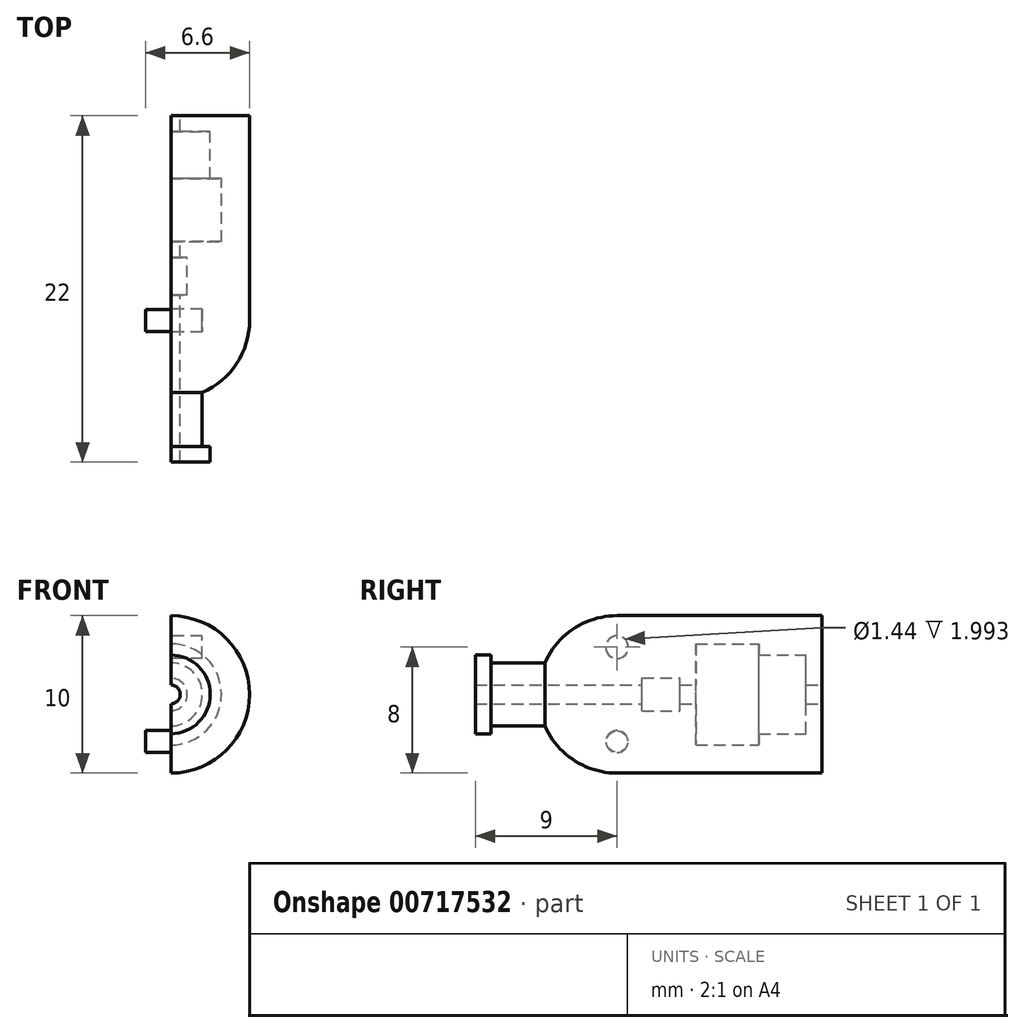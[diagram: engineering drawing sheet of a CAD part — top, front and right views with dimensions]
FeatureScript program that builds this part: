
annotation { "Feature Type Name" : "Feature", "Feature Type Description" : "" }
export const myFeature = defineFeature(function(context is Context, id is Id, definition is map)
    precondition{}
    {
        {
            var Q0;
            Q0=qCreatedBy(makeId("Front.planeOp"),FACE);
            var sketch = newSketch(context, id + "F0", { "sketchPlane" : qUnion([Q0])});
            skLineSegment(sketch, "E0", {"start": v(0, 5) * mm, "end": v(0, 5) * mm});
            skArc(sketch, "E1", {"start": v(0.01, -5) * mm, "mid": v(5, 0) * mm, "end": v(0, 5) * mm});
            skArc(sketch, "E2", {"start": v(0, 5) * mm, "mid": v(-5, 0) * mm, "end": v(0.01, -5) * mm});
            skLineSegment(sketch, "E3", {"start": v(0.01, -5) * mm, "end": v(0.01, -5) * mm});
            skLineSegment(sketch, "E4", {"start": v(0, 5) * mm, "end": v(0.01, -5) * mm});
            skSolve(sketch);
        }
        {
            var Q0;
            Q0=qCreatedBy(makeId("Front.planeOp"),FACE);
            var sketch = newSketch(context, id + "F1", { "sketchPlane" : qUnion([Q0])});
            skCircle(sketch, "E5", {"center": v(0, 0) * mm, "radius": 2 * mm});
            skSolve(sketch);
        }
        {
            var Q0;
            Q0=qCreatedBy(makeId("Front.planeOp"),FACE);
            var sketch = newSketch(context, id + "F2", { "sketchPlane" : qUnion([Q0])});
            skCircle(sketch, "E6", {"center": v(0, 0) * mm, "radius": 2.5 * mm});
            skSolve(sketch);
        }
        {
            var Q0;
            Q0 = qSketchRegion(id + "F0", true);
            var Q1;
            Q1 = qSketchRegion(id + "F10", true);
            extrude(context, id + "F3", {"entities" : qUnion([Q0, Q1]), "depth" : 18 * mm, "offsetDistance" : 25 * mm});
        }
        {
            var Q0;
            Q0=makeQuery(id+"F3.opExtrude","CAP_FACE",FACE,{"disambiguationData":[OSD([sQuery(id+"F0.wireOp",EDGE,"hpv3EBvw-azX5-sWzc-IP0I-4SNIJudsjbpc")])],"isStart":true});
            var Q1;
            Q1=makeQuery(id+"F3.opExtrude","CAP_FACE",FACE,{"disambiguationData":[OSD([sQuery(id+"F0.wireOp",EDGE,"E1"),sQuery(id+"F0.wireOp",EDGE,"E2")])],"isStart":false});
            fillet(context, id + "F4", {"entities" : qUnion([Q0, Q1]), "radius" : 5 * mm, "tangentPropagation" : true, "allowEdgeOverflow" : false});
        }
        {
            var Q0;
            Q0 = qSketchRegion(id + "F1", true);
            extrude(context, id + "F5", {"entities" : qUnion([Q0]), "operationType" : NewBodyOperationType.ADD, "depth" : 21 * mm, "offsetDistance" : 25 * mm, "hasSecondDirection" : true, "secondDirectionOppositeDirection" : false, "secondDirectionDepth" : 16 * mm});
        }
        {
            var Q0;
            Q0=makeQuery(id+"F2.imprint","IMPRINT",FACE,{"disambiguationData":[TD([[makeQuery(id+"F2.imprint","IMPRINT",EDGE,{"derivedFrom":sQuery(id+"F2.wireOp",EDGE,"E6")}),1.0]])]});
            extrude(context, id + "F6", {"entities" : qUnion([Q0]), "operationType" : NewBodyOperationType.ADD, "depth" : 22 * mm, "offsetDistance" : 25 * mm, "hasSecondDirection" : true, "secondDirectionOppositeDirection" : false, "secondDirectionDepth" : 21 * mm});
        }
        {
            var Q0;
            Q0=makeQuery(id+"F0.imprint","IMPRINT",FACE,{"disambiguationData":[TD([[makeQuery(id+"F0.imprint","IMPRINT",EDGE,{"derivedFrom":sQuery(id+"F0.wireOp",EDGE,"E2")}),1.0]])]});
            var Q1;
            Q1=sQuery(id+"F0.wireOp",EDGE,"E2");
            extrude(context, id + "F7", {"entities" : qUnion([Q0]), "operationType" : NewBodyOperationType.REMOVE, "surfaceEntities" : qUnion([Q1]), "endBound" : BoundingType.SYMMETRIC, "oppositeDirection" : true, "depth" : 46 * mm, "offsetDistance" : 25 * mm});
        }
        {
            var Q0;
            Q0=makeQuery(id+"F0.imprint","IMPRINT",FACE,{"disambiguationData":[TD([[makeQuery(id+"F0.imprint","IMPRINT",EDGE,{"derivedFrom":sQuery(id+"F0.wireOp",EDGE,"E1")}),1.0]])]});
            var sketch = newSketch(context, id + "F8", { "sketchPlane" : qUnion([Q0])});
            skCircle(sketch, "E7", {"center": v(0, 0) * mm, "radius": 3.22 * mm});
            skSolve(sketch);
        }
        {
            var Q0;
            {var subQ0=sQuery(id+"F8.wireOp",EDGE,"E7");var subQ1=makeQuery(id+"F0.imprint","IMPRINT",EDGE,{"derivedFrom":sQuery(id+"F0.wireOp",EDGE,"E4")});var subQ2=makeQuery(id+"F8.imprint","INTERSECT",VERTEX,{"disambiguationData":[OD(0.0)],"derivedFrom":[subQ1,subQ0]});Q0=makeQuery(id+"F8.imprint","IMPRINT",FACE,{"disambiguationData":[TD([[makeQuery(id+"F8.imprint","IMPRINT",EDGE,{"disambiguationData":[TD([[subQ2,-1.0]])],"derivedFrom":subQ0}),1.0]])]});}
            extrude(context, id + "F9", {"entities" : qUnion([Q0]), "operationType" : NewBodyOperationType.REMOVE, "depth" : 8 * mm, "offsetDistance" : 25 * mm, "hasSecondDirection" : true, "secondDirectionOppositeDirection" : false, "secondDirectionDepth" : 4 * mm});
        }
        {
            var Q0;
            Q0=qCreatedBy(makeId("Front.planeOp"),FACE);
            var sketch = newSketch(context, id + "F10", { "sketchPlane" : qUnion([Q0])});
            skCircle(sketch, "E8", {"center": v(0, 0) * mm, "radius": 0.6 * mm});
            skSolve(sketch);
        }
        {
            var Q0;
            Q0 = qSketchRegion(id + "F10", true);
            extrude(context, id + "F11", {"entities" : qUnion([Q0]), "operationType" : NewBodyOperationType.REMOVE, "depth" : 25 * mm, "offsetDistance" : 25 * mm});
        }
        {
            var Q0;
            Q0=qCreatedBy(makeId("Front.planeOp"),FACE);
            var sketch = newSketch(context, id + "F12", { "sketchPlane" : qUnion([Q0])});
            skCircle(sketch, "E9", {"center": v(0, 0) * mm, "radius": 2.5 * mm});
            skSolve(sketch);
        }
        {
            var Q0;
            Q0=makeQuery(id+"F12.imprint","IMPRINT",FACE,{"disambiguationData":[TD([[makeQuery(id+"F12.imprint","IMPRINT",EDGE,{"derivedFrom":sQuery(id+"F12.wireOp",EDGE,"E9")}),1.0]])]});
            extrude(context, id + "F13", {"entities" : qUnion([Q0]), "operationType" : NewBodyOperationType.REMOVE, "depth" : 4 * mm, "offsetDistance" : 25 * mm, "hasSecondDirection" : true, "secondDirectionOppositeDirection" : false, "secondDirectionDepth" : 1 * mm});
        }
        {
            var Q0;
            Q0=qCreatedBy(makeId("Front.planeOp"),FACE);
            var sketch = newSketch(context, id + "F14", { "sketchPlane" : qUnion([Q0])});
            skCircle(sketch, "E10", {"center": v(0, 0) * mm, "radius": 1.04 * mm});
            skSolve(sketch);
        }
        {
            var Q0;
            Q0 = qSketchRegion(id + "F14", true);
            var Q1;
            Q1 = qSketchRegion(id + "F16", true);
            extrude(context, id + "F15", {"entities" : qUnion([Q0, Q1]), "operationType" : NewBodyOperationType.REMOVE, "depth" : 11.4 * mm, "offsetDistance" : 25 * mm, "hasSecondDirection" : true, "secondDirectionOppositeDirection" : false, "secondDirectionDepth" : 9 * mm});
        }
        {
            var Q0;
            Q0=qCreatedBy(makeId("Right.planeOp"),FACE);
            var sketch = newSketch(context, id + "F16", { "sketchPlane" : qUnion([Q0])});
            skCircle(sketch, "E11", {"center": v(-13, -3) * mm, "radius": 0.7 * mm});
            skSolve(sketch);
        }
        {
            var Q0;
            Q0=makeQuery(id+"F16.imprint","IMPRINT",FACE,{"disambiguationData":[TD([[makeQuery(id+"F16.imprint","IMPRINT",EDGE,{"derivedFrom":sQuery(id+"F16.wireOp",EDGE,"E11")}),1.0]])]});
            var Q1;
            Q1=sQuery(id+"F16.wireOp",EDGE,"E11");
            extrude(context, id + "F17", {"entities" : qUnion([Q0]), "operationType" : NewBodyOperationType.ADD, "surfaceEntities" : qUnion([Q1]), "depth" : 2 * mm, "offsetDistance" : 25 * mm, "hasSecondDirection" : true, "secondDirectionOppositeDirection" : true, "secondDirectionDepth" : 1.6 * mm});
        }
        {
            var Q0;
            Q0=qCreatedBy(makeId("Right.planeOp"),FACE);
            var sketch = newSketch(context, id + "F18", { "sketchPlane" : qUnion([Q0])});
            skCircle(sketch, "E12", {"center": v(-13, 3) * mm, "radius": 0.72 * mm});
            skSolve(sketch);
        }
        {
            var Q0;
            Q0 = qSketchRegion(id + "F18", true);
            extrude(context, id + "F19", {"entities" : qUnion([Q0]), "operationType" : NewBodyOperationType.REMOVE, "depth" : 2 * mm, "offsetDistance" : 25 * mm});
        }
    });
